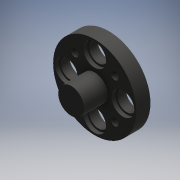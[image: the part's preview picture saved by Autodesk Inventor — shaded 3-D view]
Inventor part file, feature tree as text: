
AUTODESK INVENTOR PART (.ipt)
format: ipt  version: 2016 (Build 200138000, 138)  size: 189,952 bytes
history: native  units: mm
features: extrude x4, sketch x4, plane x1, mirror x1
ambient origin geometry x8: Origin, YZ Plane, XZ Plane, XY Plane, X Axis, Y Axis, Z Axis, Center Point
bodies: Solid1 (feature_tree)
feature tree (10):
  extrude  "Extrusion1"  Depth=3.0mm TaperAngle=0.0deg
  extrude  "Extrusion2"  Depth=5.0mm TaperAngle=0.0deg
  extrude  "Extrusion3"  Depth=6.0mm
  extrude  "Extrusion4"  Depth=5.0mm TaperAngle=0.0deg
  plane  "Work Plane1"
  mirror  "Mirror1"
  sketch  "Sketch1"  dims[d0=17.65mm d1=3.0mm d2=0.0mm]
  sketch  "Sketch2"  dims[d3=5.5mm d4=5.0mm d5=0.0mm]
  sketch  "Sketch3"  dims[d6=4.0mm d7=6.0mm]
  sketch  "Sketch4"  dims[d8=40.0mm d10=360.0deg d12=5.0mm d13=0.0mm d14=1.6mm d15=45.0deg d16=40.0mm d18=360.0deg d20=0.4mm d21=0.4mm d22=0.4mm d23=0.4mm d24=0.8mm d25=0.0mm]
